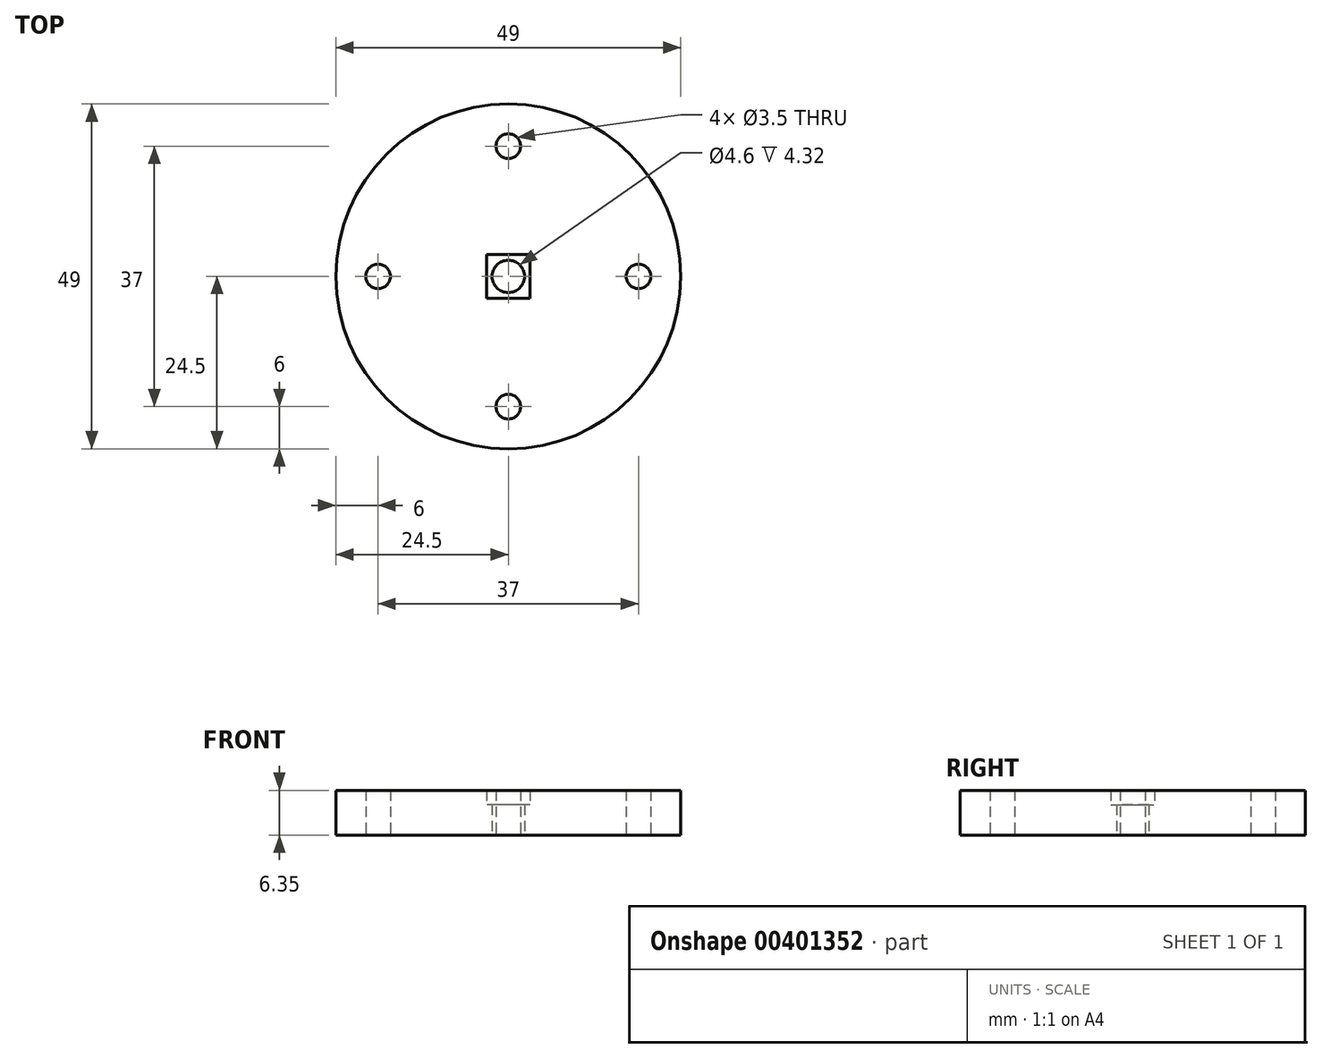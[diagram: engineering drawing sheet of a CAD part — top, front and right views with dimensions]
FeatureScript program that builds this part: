
annotation { "Feature Type Name" : "Feature", "Feature Type Description" : "" }
export const myFeature = defineFeature(function(context is Context, id is Id, definition is map)
    precondition{}
    {
        {
            var Q0;
            Q0=qCreatedBy(makeId("Top.planeOp"),FACE);
            var sketch = newSketch(context, id + "F0", { "sketchPlane" : qUnion([Q0])});
            skCircle(sketch, "E0", {"center": v(0, 0) * mm, "radius": 24.5 * mm});
            skLineSegment(sketch, "E1.bottom", {"start": v(3.1, -3.1) * mm, "end": v(-3.1, -3.1) * mm});
            skLineSegment(sketch, "E1.top", {"start": v(3.1, 3.1) * mm, "end": v(-3.1, 3.1) * mm});
            skLineSegment(sketch, "E1.left", {"start": v(3.1, -3.1) * mm, "end": v(3.1, 3.1) * mm});
            skLineSegment(sketch, "E1.right", {"start": v(-3.1, -3.1) * mm, "end": v(-3.1, 3.1) * mm});
            skCircle(sketch, "E2", {"center": v(0, 0) * mm, "radius": 2.3 * mm});
            skLineSegment(sketch, "E3", {"start": v(-24.5, 0) * mm, "end": v(24.5, 0) * mm, "construction": true});
            skPoint(sketch, "E3.endSnap0", {"position": v(3.1, 0) * mm});
            skLineSegment(sketch, "E4", {"start": v(0, 24.5) * mm, "end": v(0, -24.5) * mm, "construction": true});
            skPoint(sketch, "E4.startSnap0", {"position": v(0, 3.1) * mm});
            skCircle(sketch, "E5", {"center": v(18.5, 0) * mm, "radius": 1.75 * mm});
            skCircle(sketch, "E6", {"center": v(0, 18.5) * mm, "radius": 1.75 * mm});
            skCircle(sketch, "E7", {"center": v(-18.5, 0) * mm, "radius": 1.75 * mm});
            skCircle(sketch, "E8", {"center": v(0, -18.5) * mm, "radius": 1.75 * mm});
            skSolve(sketch);
        }
        {
            var Q0;
            Q0=makeQuery(id+"F0.imprint","IMPRINT",FACE,{"disambiguationData":[TD([[makeQuery(id+"F0.imprint","IMPRINT",EDGE,{"derivedFrom":sQuery(id+"F0.wireOp",EDGE,"E0")}),1.0]])]});
            extrude(context, id + "F1", {"entities" : qUnion([Q0]), "depth" : 6.35 * mm, "offsetDistance" : 25 * mm});
        }
        {
            var Q0;
            Q0=makeQuery(id+"F0.imprint","IMPRINT",FACE,{"disambiguationData":[TD([[makeQuery(id+"F0.imprint","IMPRINT",EDGE,{"derivedFrom":sQuery(id+"F0.wireOp",EDGE,"E1.bottom")}),-1.0]])]});
            extrude(context, id + "F2", {"entities" : qUnion([Q0]), "operationType" : NewBodyOperationType.ADD, "depth" : 4.32 * mm, "offsetDistance" : 25 * mm});
        }
    });
